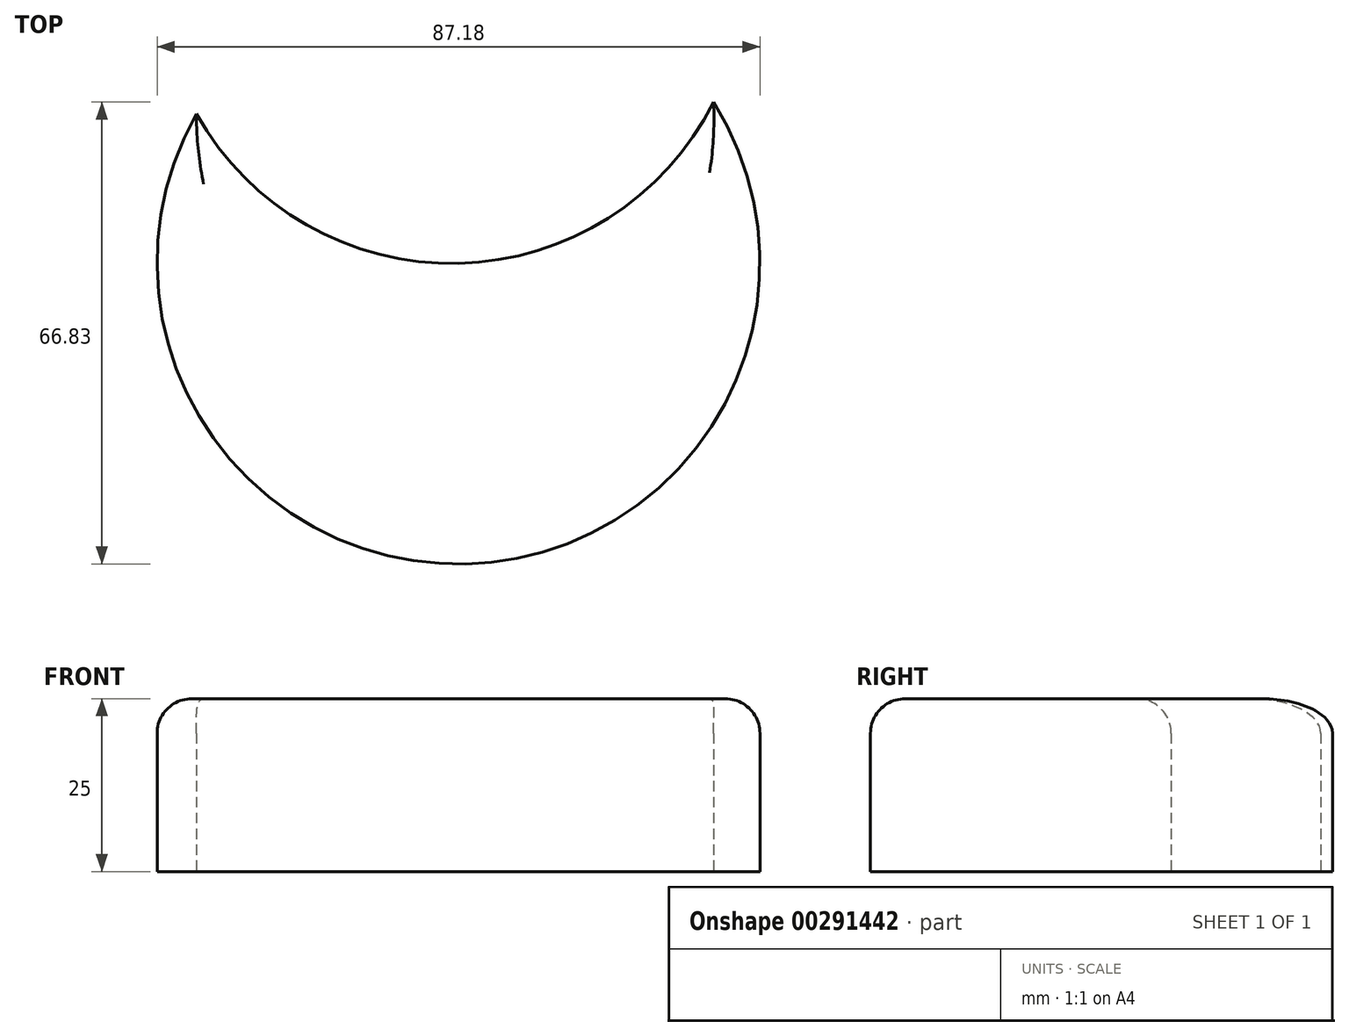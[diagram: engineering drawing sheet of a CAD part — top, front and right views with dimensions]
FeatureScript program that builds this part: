
annotation { "Feature Type Name" : "Feature", "Feature Type Description" : "" }
export const myFeature = defineFeature(function(context is Context, id is Id, definition is map)
    precondition{}
    {
        {
            var Q0;
            Q0=qCreatedBy(makeId("Top.planeOp"),FACE);
            var sketch = newSketch(context, id + "F0", { "sketchPlane" : qUnion([Q0])});
            skArc(sketch, "E0", {"start": v(-39.94, 36.54) * mm, "mid": v(-1.05, -28.58) * mm, "end": v(34.84, 38.24) * mm});
            skArc(sketch, "E1", {"start": v(-39.94, 36.54) * mm, "mid": v(-2.04, 14.91) * mm, "end": v(34.84, 38.24) * mm});
            skSolve(sketch);
        }
        {
            var Q0;
            Q0=makeQuery(id+"F0.imprint","IMPRINT",FACE,{"disambiguationData":[TD([[makeQuery(id+"F0.imprint","IMPRINT",EDGE,{"derivedFrom":sQuery(id+"F0.wireOp",EDGE,"E0")}),1.0]])]});
            var sketch = newSketch(context, id + "F1", { "sketchPlane" : qUnion([Q0])});
            skSolve(sketch);
        }
        {
            var Q0;
            Q0 = qSketchRegion(id + "F1", true);
            var Q1;
            Q1=makeQuery(id+"F0.imprint","IMPRINT",FACE,{"disambiguationData":[TD([[makeQuery(id+"F0.imprint","IMPRINT",EDGE,{"derivedFrom":sQuery(id+"F0.wireOp",EDGE,"E0")}),1.0]])]});
            extrude(context, id + "F2", {"entities" : qUnion([Q0, Q1]), "depth" : 25 * mm});
        }
        {
            var Q0;
            Q0=makeQuery(id+"F2.opExtrude","CAP_EDGE",EDGE,{"disambiguationData":[OSD([sQuery(id+"F0.wireOp",EDGE,"E0")])],"isStart":false});
            var Q1;
            Q1=makeQuery(id+"F2.opExtrude","CAP_EDGE",EDGE,{"disambiguationData":[OSD([sQuery(id+"F0.wireOp",EDGE,"E1")])],"isStart":false});
            fillet(context, id + "F3", {"entities" : qUnion([Q0, Q1]), "radius" : 5 * mm, "tangentPropagation" : true, "allowEdgeOverflow" : false});
        }
    });
